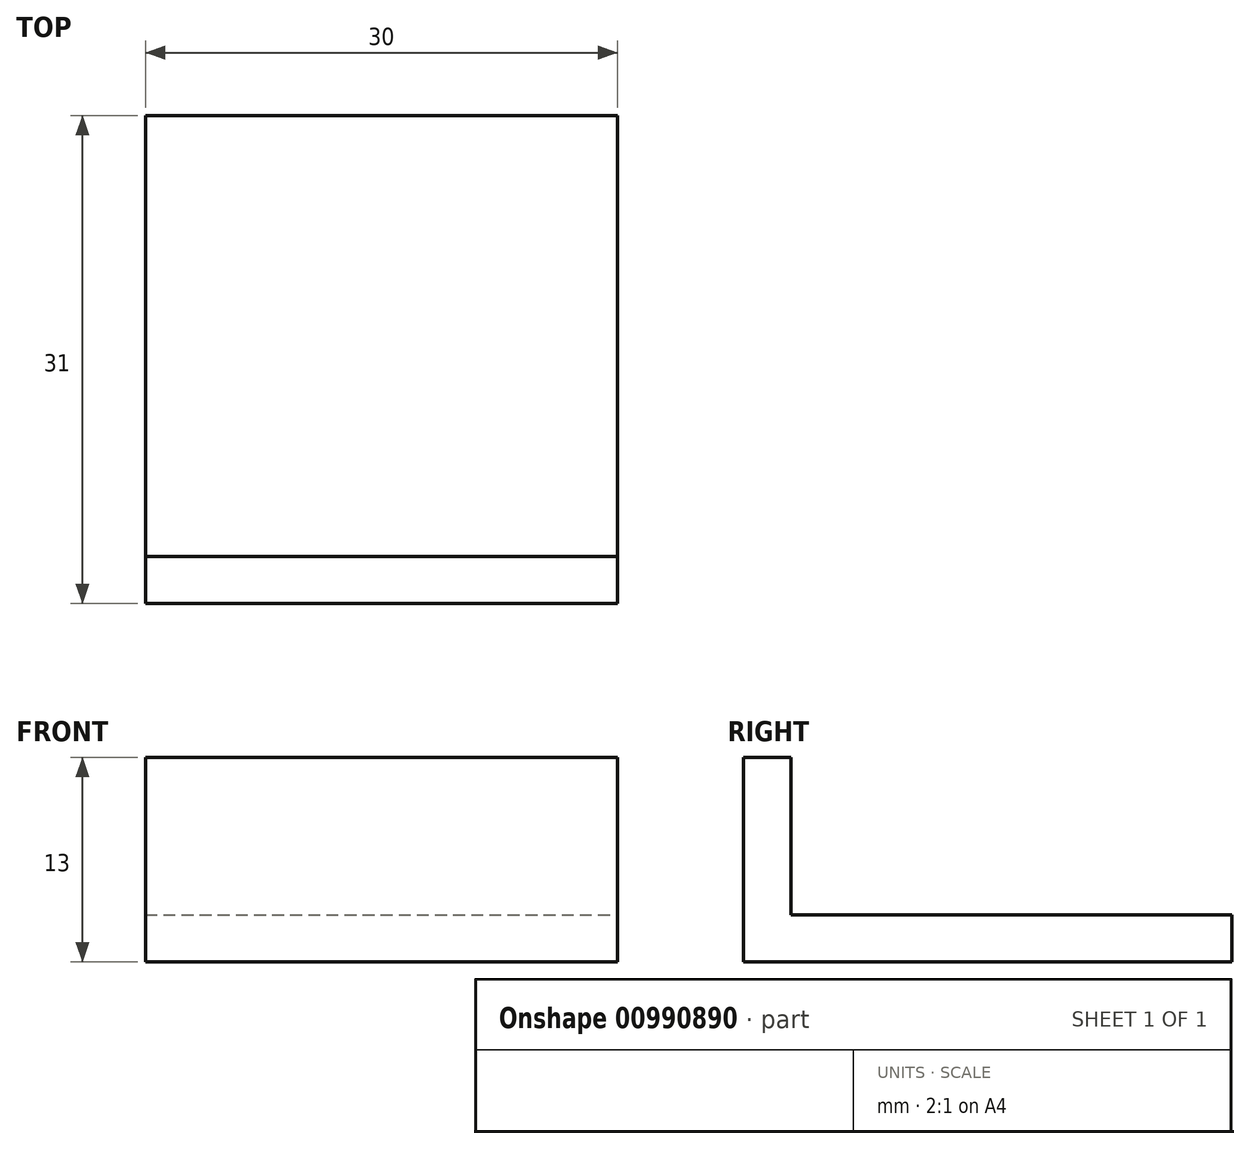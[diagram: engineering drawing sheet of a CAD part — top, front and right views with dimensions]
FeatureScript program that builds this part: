
annotation { "Feature Type Name" : "Feature", "Feature Type Description" : "" }
export const myFeature = defineFeature(function(context is Context, id is Id, definition is map)
    precondition{}
    {
        {
            var Q0;
            Q0=qCreatedBy(makeId("Top.planeOp"),FACE);
            var sketch = newSketch(context, id + "F0", { "sketchPlane" : qUnion([Q0])});
            skLineSegment(sketch, "E0.bottom", {"start": v(-15, 15.5) * mm, "end": v(15, 15.5) * mm});
            skLineSegment(sketch, "E0.top", {"start": v(-15, -15.5) * mm, "end": v(15, -15.5) * mm});
            skLineSegment(sketch, "E0.left", {"start": v(-15, 15.5) * mm, "end": v(-15, -15.5) * mm});
            skLineSegment(sketch, "E0.right", {"start": v(15, 15.5) * mm, "end": v(15, -15.5) * mm});
            skPoint(sketch, "E0.middle", {"position": v(0, 0) * mm});
            skSolve(sketch);
        }
        {
            var Q0;
            Q0 = qSketchRegion(id + "F0", true);
            extrude(context, id + "F1", {"entities" : qUnion([Q0]), "depth" : 3 * mm, "offsetDistance" : 25 * mm});
        }
        {
            var Q0;
            Q0=makeQuery(id+"F1.opExtrude","CAP_FACE",FACE,{"disambiguationData":[OSD([sQuery(id+"F0.wireOp",EDGE,"E0.bottom"),sQuery(id+"F0.wireOp",EDGE,"E0.top"),sQuery(id+"F0.wireOp",EDGE,"E0.left"),sQuery(id+"F0.wireOp",EDGE,"E0.right")])],"isStart":false});
            var sketch = newSketch(context, id + "F2", { "sketchPlane" : qUnion([Q0])});
            skLineSegment(sketch, "E1.bottom", {"start": v(-15, -15.5) * mm, "end": v(15, -15.5) * mm});
            skLineSegment(sketch, "E1.top", {"start": v(-15, -12.5) * mm, "end": v(15, -12.5) * mm});
            skLineSegment(sketch, "E1.left", {"start": v(-15, -15.5) * mm, "end": v(-15, -12.5) * mm});
            skLineSegment(sketch, "E1.right", {"start": v(15, -15.5) * mm, "end": v(15, -12.5) * mm});
            skSolve(sketch);
        }
        {
            var Q0;
            Q0=makeQuery(id+"F2.imprint","IMPRINT",FACE,{"disambiguationData":[TD([[makeQuery(id+"F2.imprint","IMPRINT",EDGE,{"derivedFrom":sQuery(id+"F2.wireOp",EDGE,"E1.bottom")}),1.0]])]});
            extrude(context, id + "F3", {"entities" : qUnion([Q0]), "operationType" : NewBodyOperationType.ADD, "depth" : 10 * mm, "offsetDistance" : 25 * mm});
        }
    });
